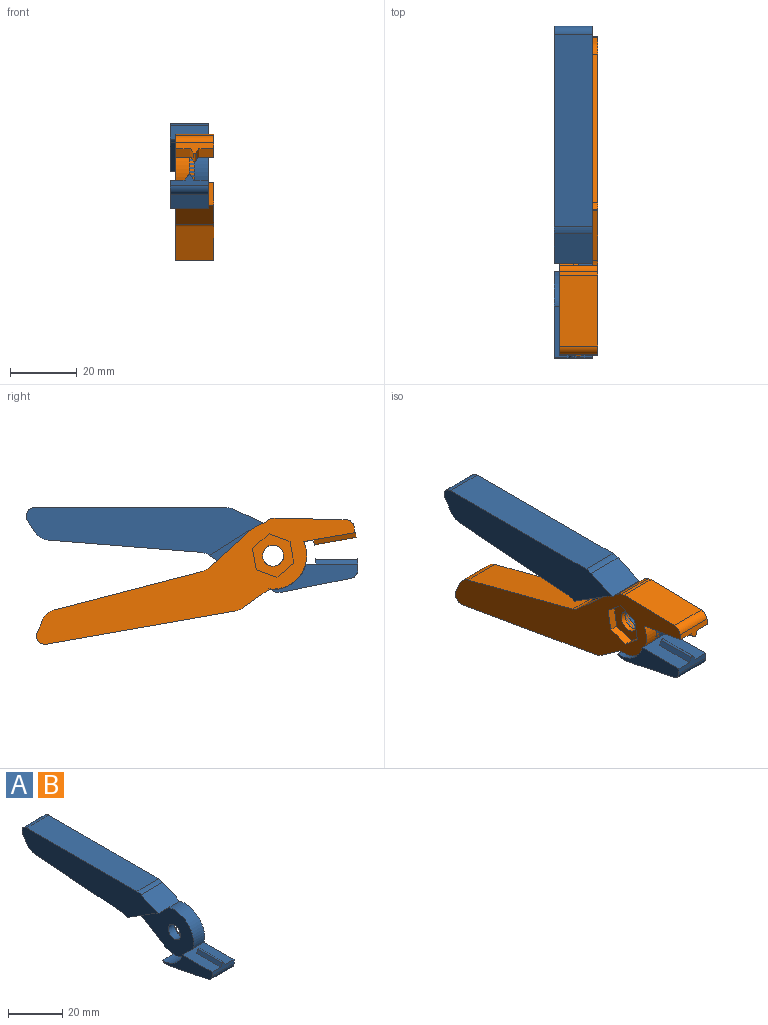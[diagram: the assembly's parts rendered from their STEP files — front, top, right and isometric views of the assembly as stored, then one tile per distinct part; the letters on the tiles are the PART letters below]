
ASSEMBLY  parts=2 mates=1
PART A: 37 faces, bbox 11.4x99.4x25.3 mm
  f0: plane 99.39x25.33mm, normal (1,0,0), area 1110.8mm2, adj f2,f3,f4,f5,f6,f7,f9,f10
  f1: cylinder r=3.17mm len=6.35mm, axis (-1,0,0), area 63.3mm2, adj f16,f36
  f2: plane 5.72x0.17mm, normal (0,-0.83,-0.55), area 1.1mm2, adj f0,f7,f13,f16
  f3: plane 13.38x11.43mm, normal (0,0.53,-0.85), area 92.5mm2, adj f0,f8,f9,f15,f16,f18
  f4: plane 45.76x11.43mm, normal (0,0.08,-1), area 524.7mm2, adj f0,f8,f9,f10
  f5: plane 11.43x3.51mm, normal (0,0.83,-0.56), area 48.2mm2, adj f0,f8,f10,f12
  f6: plane 57.51x11.43mm, normal (0,0,1), area 657.4mm2, adj f0,f8,f11,f12
  f7: plane 11.43x8.86mm, normal (0,-0.42,0.91), area 111.8mm2, adj f0,f2,f8,f11,f17
  f8: plane 71.07x14.33mm, normal (-1,0,0), area 738.1mm2, adj f3,f4,f5,f6,f7,f9,f10,f11
  f9: cylinder r=5.08mm len=11.43mm, axis (-1,0,0), area 28.1mm2, adj f0,f3,f4,f8
  f10: cylinder r=5.08mm len=11.43mm, axis (-1,0,0), area 52.4mm2, adj f0,f4,f5,f8
  f11: cylinder r=5.08mm len=11.43mm, axis (-1,0,0), area 25.4mm2, adj f0,f6,f7,f8
  f12: cylinder r=2.54mm len=11.43mm, axis (-1,0,0), area 62.7mm2, adj f0,f5,f6,f8
  f13: cylinder r=10.03mm len=13.06mm, axis (-1,0,0), area 122.3mm2, adj f0,f2,f14,f16
  f14: plane 15.69x11.43mm, normal (0,0,1), area 146.4mm2, adj f0,f13,f16,f19,f20,f23,f26,f27
  f15: cylinder r=10.16mm len=5.72mm, axis (-1,0,0), area 33.3mm2, adj f0,f3,f16,f25
  f16: plane 29.06x20.19mm, normal (-1,0,0), area 349.2mm2, adj f1,f2,f3,f13,f14,f15,f17,f18
  f17: cylinder r=10.16mm len=5.72mm, axis (1,0,0), area 15.7mm2, adj f7,f8,f16,f18
  f18: plane 13.61x8.57mm, normal (0,-0.53,-0.85), area 91.9mm2, adj f3,f8,f16,f17
  f19: cylinder r=10.16mm len=10.38mm, axis (-1,0,0), area 79.6mm2, adj f14,f16,f23,f25
  f20: plane 11.43x3.39mm, normal (0,-1,0), area 22.4mm2, adj f0,f14,f23,f24,f26,f27,f29
  f21: plane 20.84x11.43mm, normal (0,-0.2,-0.98), area 243mm2, adj f0,f22,f23,f24
  f22: plane 11.43x1.19mm, normal (0,0,-1), area 13.6mm2, adj f0,f21,f23,f25
  f23: plane 25.94x8.43mm, normal (-1,0,0), area 105mm2, adj f14,f19,f20,f21,f22,f24,f25
  f24: cylinder r=2.54mm len=11.43mm, axis (-1,0,0), area 39.8mm2, adj f0,f20,f21,f23
  f25: cylinder r=2.54mm len=11.43mm, axis (-1,0,0), area 24.1mm2, adj f0,f15,f19,f22,f23
  f26: plane 12.7x1.4mm, normal (0.86,0,0.51), area 20.6mm2, adj f14,f20,f28,f29
  f27: plane 12.7x1.4mm, normal (-0.86,0,0.51), area 20.6mm2, adj f14,f20,f28,f29
  f28: plane 2.54x1.64mm, normal (0,1,0), area 2.5mm2, adj f14,f26,f27,f29
  f29: cylinder r=0.51mm len=12.7mm, axis (0,-1,0), area 13.3mm2, adj f20,f26,f27,f28
  f30: plane 5.72x3.3mm, normal (0,-0.5,-0.87), area 16.8mm2, adj f0,f31,f35,f36
  f31: plane 5.72x3.3mm, normal (0,0.5,-0.87), area 16.8mm2, adj f0,f30,f32,f36
  f32: plane 6.6x2.54mm, normal (0,1,0), area 16.8mm2, adj f0,f31,f33,f36
  f33: plane 5.72x3.3mm, normal (0,0.5,0.87), area 16.8mm2, adj f0,f32,f34,f36
  f34: plane 5.72x3.3mm, normal (0,-0.5,0.87), area 16.8mm2, adj f0,f33,f35,f36
  f35: plane 6.6x2.54mm, normal (0,-1,0), area 16.8mm2, adj f0,f30,f34,f36
  f36: plane 13.2x11.43mm, normal (1,0,0), area 81.5mm2, adj f1,f30,f31,f32,f33,f34,f35
PART B: same geometry as A
PLACE A t=(18.33,-31.42,-2.32)mm
PLACE B rot(axis=(0,-1,0.09),180deg) t=(19.92,-31.42,-2.32)mm
MATE revolute B.f1 <-> A.f1  axis (1,0,0) through (18.33,-31.42,-2.32)mm
